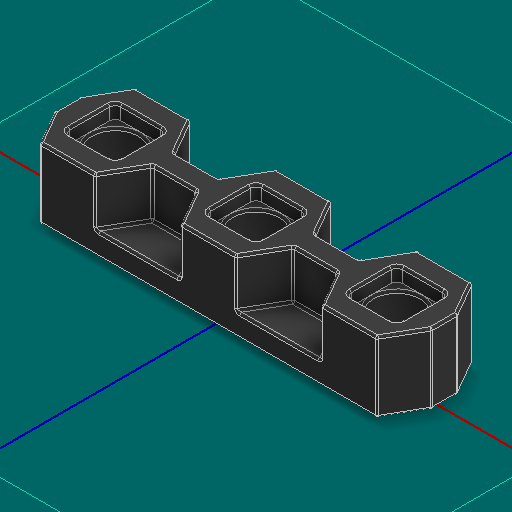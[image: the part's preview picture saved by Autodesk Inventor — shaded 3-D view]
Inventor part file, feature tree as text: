
AUTODESK INVENTOR PART (.ipt)
format: ipt  version: 2025 (Build 290162000, 162)  size: 504,320 bytes
history: native  units: in
note: dims shown in document units (in); Inventor stores cm internally (conversion verified against a paired STEP export)
features: other x3, sketch x1
ambient origin geometry x8: Origin, YZ Plane, XZ Plane, XY Plane, X Axis, Y Axis, Z Axis, Center Point
bodies: Solid1 (feature_tree)
feature tree (4):
  other  "Bearing Flat Low Profile.ipt"
  other  "Solid1::Bearing Flat Low Profile.ipt"
  other  "TaggingFeature1"
  sketch  "Sketch1"  dims[d0=0.3937in]
